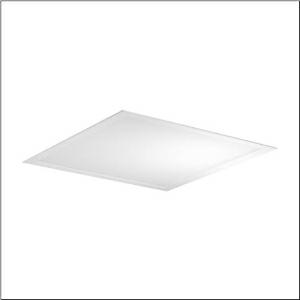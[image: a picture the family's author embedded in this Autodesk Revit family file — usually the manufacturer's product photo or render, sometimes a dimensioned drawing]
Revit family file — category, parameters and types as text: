
# Revit family: apollon_21_square_51mq11wd2m14
name_source: partatom
category: Lighting Fixtures
units: mm (PartAtom-declared; Revit-internal decimal feet)

## family parameters
Cut with Voids When Loaded = No
Host = Face
Light Source = No
Part Type = Normal
Room Calculation Point = No
Round Connector Dimension = Use Diameter
Shared = No

## types (1)
- --- (1 x LED, 4200 lm, 26 W, 4000K)
    Apparent Load = 26 VA
    CIE Flux Codes = 60 87 97 100 100
    Color Rendering = 80
    Color Temperature = 4000K
    Default Elevation = 1800 mm
    Description = Apollon 21 square, office luminaire, primary optical cover: micro prismatic cover, of PMMA, CAT 2 (L<= 3000cd/m²), light emission: direct distribution, primary light characteristic: symmetric, installation type: lay-in mounting, LED, rated luminous flux: 4.200lm, luminous efficacy: 162lm/W, light colour: 830/840, colour temperature: 3000/4000K, control gear: DALI 2, Multilumen, with terminal, 5-pole, mains connection: 220..240V, AC/DC, 0/50..60Hz, rated input power: 26W, suitable for self-contained emergency lighting element 59MQE002602A with integrated self-test function according to EN 60598-2-22, housing, of aluminium, coated, traffic white (RAL 9016), module: M625, length: 620mm, width: 620mm, height: 55mm, recess depth: 180mm, housing upper side, of sheet steel, galvanised, protection rating (complete): IP20, protection rating (lamp compartment, on room side): IP50, insulation class (complete): insulation class II (safety insulation), certification: CE, ENEC, impact resistance: IK03, permissible operating ambient temperature: -20..+45°C, permissible storage temperature: -40..+80°C, standard: EN 60598-2-22, packaging unit: 1 piece
    Height = 0 mm  [stored 0 ft]
    Lamp = 1 x LED
    Lamp Light Flux = 4200 lm
    Lamp Power = 26 W
    Lamp count = 1
    Length = 620 mm
    Luminous efficacy = 162 lm/W
    Manufacturer = Siteco
    ModVariant = No
    Model = 51MQ11WD2M14
    Mounting Place = Ceiling
    Mounting Type = Recessed
    Number of Poles = 1
    OnlyDefault = Yes
    Power Factor = 1
    Product Name = Apollon 21 square
    Product group = office luminaire | ceiling recessed
    ProductGroupID = 400
    Protection Class = Protection class II
    Protection Degree = IP 20
    RLX_Detail_Level = 1
    RLX_Emergency_Light_Flux = 0 lm
    RLX_Emergency_Type = 0
    RLX_Emergency_Type_DB = No
    RlxData = <blob elided: 13361 chars, md5=6f9d0241>
    Socket = socket
    Standby Power = 0 W
    System Light Flux = 4200 lm
    System Power = 26 W
    Type Comments = factory setting
    Type Image = l_1291054.jpg
    URL = http://relux.com
    VarID = @adj_089641
    Voltage = 0 V
    Weight = 0.00 kg
    Width = 620 mm

note: [stored X ft] marks values corroborated as IEEE doubles in the binary element streams (Revit-internal decimal feet)

## geometry (parser evidence)
native form markers: Sweep x10
no freeform markers — native parametric forms only
